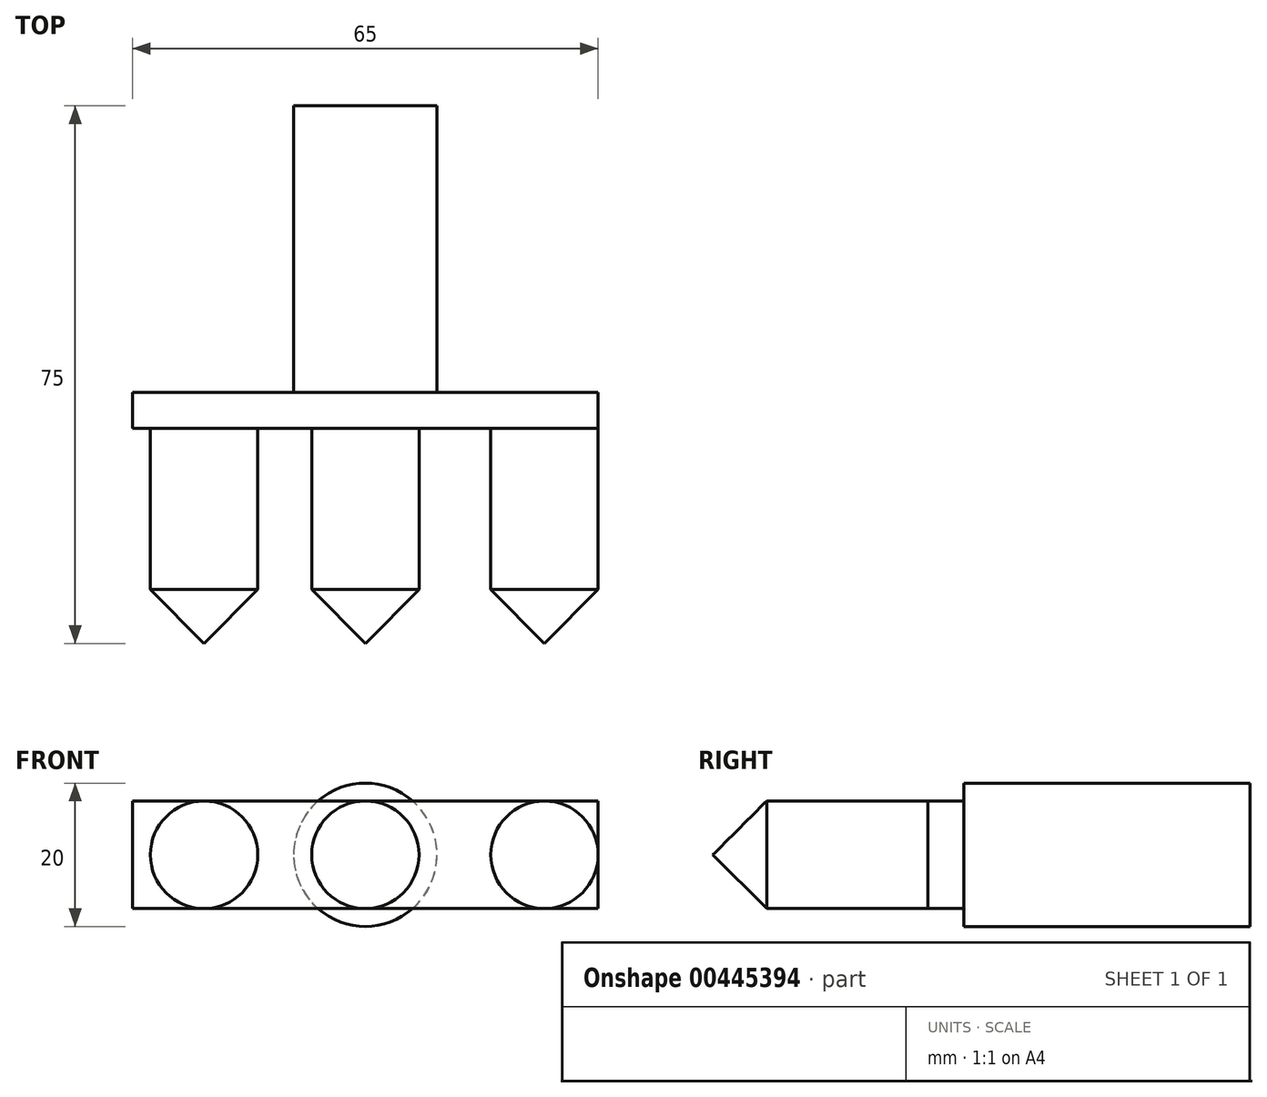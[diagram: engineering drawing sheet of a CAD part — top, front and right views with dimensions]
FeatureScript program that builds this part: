
annotation { "Feature Type Name" : "Feature", "Feature Type Description" : "" }
export const myFeature = defineFeature(function(context is Context, id is Id, definition is map)
    precondition{}
    {
        {
            var Q0;
            Q0=qCreatedBy(makeId("Front.planeOp"),FACE);
            var sketch = newSketch(context, id + "F0", { "sketchPlane" : qUnion([Q0])});
            skLineSegment(sketch, "E0.bottom", {"start": v(32.5, -7.5) * mm, "end": v(-32.5, -7.5) * mm});
            skLineSegment(sketch, "E0.top", {"start": v(32.5, 7.5) * mm, "end": v(-32.5, 7.5) * mm});
            skLineSegment(sketch, "E0.left", {"start": v(32.5, -7.5) * mm, "end": v(32.5, 7.5) * mm});
            skLineSegment(sketch, "E0.right", {"start": v(-32.5, -7.5) * mm, "end": v(-32.5, 7.5) * mm});
            skPoint(sketch, "E0.middle", {"position": v(0, 0) * mm});
            skSolve(sketch);
        }
        {
            var Q0;
            Q0=makeQuery(id+"F0.imprint","IMPRINT",FACE,{"disambiguationData":[TD([[makeQuery(id+"F0.imprint","IMPRINT",EDGE,{"derivedFrom":sQuery(id+"F0.wireOp",EDGE,"E0.bottom")}),-1.0]])]});
            extrude(context, id + "F1", {"entities" : qUnion([Q0]), "depth" : 5 * mm});
        }
        {
            var Q0;
            Q0=makeQuery(id+"F1.opExtrude","CAP_FACE",FACE,{"disambiguationData":[OSD([sQuery(id+"F0.wireOp",EDGE,"E0.bottom"),sQuery(id+"F0.wireOp",EDGE,"E0.top"),sQuery(id+"F0.wireOp",EDGE,"E0.left"),sQuery(id+"F0.wireOp",EDGE,"E0.right")])],"isStart":false});
            var sketch = newSketch(context, id + "F2", { "sketchPlane" : qUnion([Q0])});
            skCircle(sketch, "E1", {"center": v(0, 0) * mm, "radius": 7.5 * mm});
            skLineSegment(sketch, "E2", {"start": v(7.5, 0) * mm, "end": v(25, 0) * mm});
            skLineSegment(sketch, "E3", {"start": v(-7.5, 0) * mm, "end": v(-22.5, 0) * mm});
            skCircle(sketch, "E4", {"center": v(-22.5, 0) * mm, "radius": 7.5 * mm});
            skCircle(sketch, "E5", {"center": v(25, 0) * mm, "radius": 7.5 * mm});
            skSolve(sketch);
        }
        {
            var Q0;
            Q0 = qSketchRegion(id + "F2", true);
            extrude(context, id + "F3", {"entities" : qUnion([Q0]), "operationType" : NewBodyOperationType.ADD, "depth" : 30 * mm});
        }
        {
            var Q0;
            Q0=makeQuery(id+"F1.opExtrude","CAP_FACE",FACE,{"disambiguationData":[OSD([sQuery(id+"F0.wireOp",EDGE,"E0.bottom"),sQuery(id+"F0.wireOp",EDGE,"E0.top"),sQuery(id+"F0.wireOp",EDGE,"E0.left"),sQuery(id+"F0.wireOp",EDGE,"E0.right")])],"isStart":true});
            var sketch = newSketch(context, id + "F4", { "sketchPlane" : qUnion([Q0])});
            skCircle(sketch, "E6", {"center": v(0, 0) * mm, "radius": 10 * mm});
            skSolve(sketch);
        }
        {
            var Q0;
            {var subQ0=sQuery(id+"F4.wireOp",EDGE,"E6");var subQ1=makeQuery(id+"F1.opExtrude","CAP_EDGE",EDGE,{"disambiguationData":[OSD([sQuery(id+"F0.wireOp",EDGE,"E0.top")])],"isStart":true});var subQ2=makeQuery(id+"F4.imprint","INTERSECT",VERTEX,{"disambiguationData":[OD(0.0)],"derivedFrom":[subQ1,subQ0]});Q0=makeQuery(id+"F4.imprint","IMPRINT",FACE,{"disambiguationData":[TD([[makeQuery(id+"F4.imprint","IMPRINT",EDGE,{"disambiguationData":[TD([[subQ2,-1.0]])],"derivedFrom":subQ0}),1.0]])]});}
            var Q1;
            {var subQ0=sQuery(id+"F4.wireOp",EDGE,"E6");var subQ1=makeQuery(id+"F1.opExtrude","CAP_EDGE",EDGE,{"disambiguationData":[OSD([sQuery(id+"F0.wireOp",EDGE,"E0.bottom")])],"isStart":true});var subQ2=makeQuery(id+"F4.imprint","INTERSECT",VERTEX,{"disambiguationData":[OD(0.0)],"derivedFrom":[subQ1,subQ0]});Q1=makeQuery(id+"F4.imprint","IMPRINT",FACE,{"disambiguationData":[TD([[makeQuery(id+"F4.imprint","IMPRINT",EDGE,{"disambiguationData":[TD([[subQ2,-1.0]])],"derivedFrom":subQ0}),1.0]])]});}
            var Q2;
            {var subQ0=sQuery(id+"F4.wireOp",EDGE,"E6");var subQ1=makeQuery(id+"F1.opExtrude","CAP_EDGE",EDGE,{"disambiguationData":[OSD([sQuery(id+"F0.wireOp",EDGE,"E0.top")])],"isStart":true});var subQ2=makeQuery(id+"F4.imprint","INTERSECT",VERTEX,{"disambiguationData":[OD(0.0)],"derivedFrom":[subQ1,subQ0]});Q2=makeQuery(id+"F4.imprint","IMPRINT",FACE,{"disambiguationData":[TD([[makeQuery(id+"F4.imprint","IMPRINT",EDGE,{"disambiguationData":[TD([[subQ2,1.0]])],"derivedFrom":subQ0}),1.0]])]});}
            extrude(context, id + "F5", {"entities" : qUnion([Q0, Q1, Q2]), "operationType" : NewBodyOperationType.ADD, "depth" : 40 * mm});
        }
        {
            var Q0;
            Q0=makeQuery(id+"F3.opExtrude","CAP_FACE",FACE,{"disambiguationData":[OSD([sQuery(id+"F2.wireOp",EDGE,"E4")])],"isStart":false});
            var Q1;
            Q1=makeQuery(id+"F3.opExtrude","CAP_FACE",FACE,{"disambiguationData":[OSD([sQuery(id+"F2.wireOp",EDGE,"E1")])],"isStart":false});
            var Q2;
            Q2=makeQuery(id+"F3.opExtrude","CAP_FACE",FACE,{"disambiguationData":[OSD([sQuery(id+"F2.wireOp",EDGE,"E5")])],"isStart":false});
            chamfer(context, id + "F6", {"entities" : qUnion([Q0, Q1, Q2]), "width" : 7.5 * mm, "tangentPropagation" : true});
        }
    });
